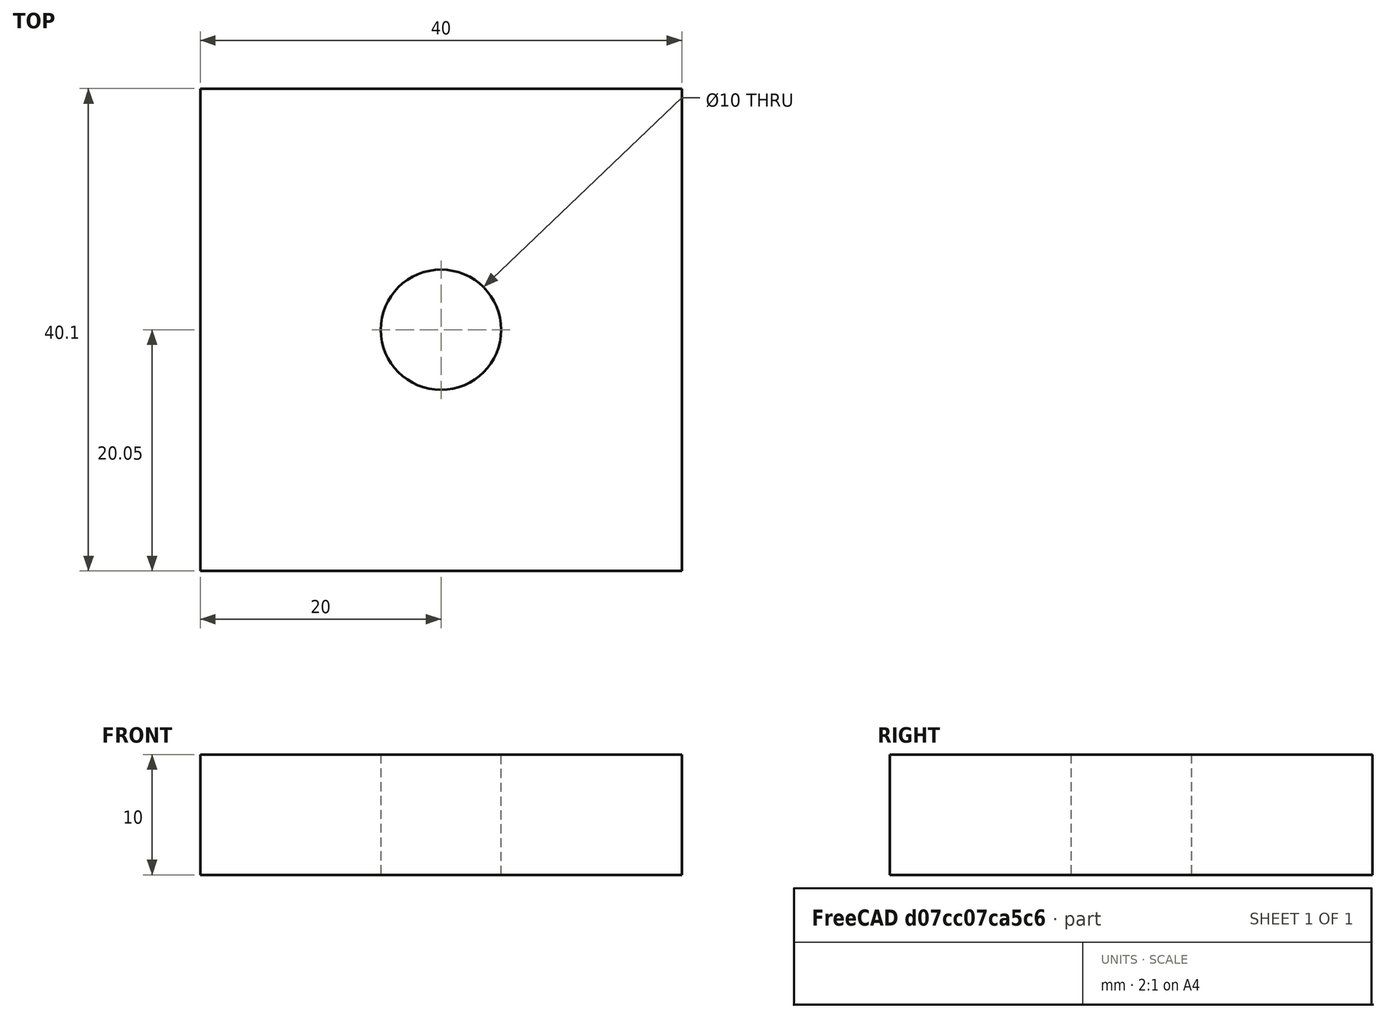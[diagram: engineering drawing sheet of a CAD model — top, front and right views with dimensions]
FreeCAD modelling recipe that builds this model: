
FCSTD DOCUMENT  (FreeCAD 0.20R29410 (Git))
Label: mola
License: All rights reserved
LicenseURL: http://en.wikipedia.org/wiki/All_rights_reserved
objects: Sketcher::SketchObject×1, Part::Extrusion×1
note: 2 computed .brp shape members not serialized (recipe doc carries the construction recipe); baked Part::Feature solids carry a one-line shape summary decoded from their .brp

FEATURE [Sketcher::SketchObject] Sketch
  FullyConstrained = true
  sketch-geometry (5):
    g0: LineSegment StartX=-20 StartY=20.045 StartZ=0 EndX=20 EndY=20.045 EndZ=0
    g1: LineSegment StartX=20 StartY=20.045 StartZ=0 EndX=20 EndY=-20.045 EndZ=0
    g2: LineSegment StartX=20 StartY=-20.045 StartZ=0 EndX=-20 EndY=-20.045 EndZ=0
    g3: LineSegment StartX=-20 StartY=-20.045 StartZ=0 EndX=-20 EndY=20.045 EndZ=0
    g4: Circle CenterX=0 CenterY=0 CenterZ=0 NormalX=0 NormalY=0 NormalZ=1 AngleXU=0 Radius=5
  constraints (13):
    c: Coincident(g0,g1)
    c: Coincident(g1,g2)
    c: Coincident(g2,g3)
    c: Coincident(g3,g0)
    c: Horizontal(g0)
    c: Horizontal(g2)
    c: Vertical(g1)
    c: Vertical(g3)
    c: Symmetric(g1,g0,g-1)
    c: DistanceX(g0,g0) = 40  'a'
    c: DistanceY(g1,g1) = 40.09  'b'
    c: Diameter(g4) = 10  'd'
    c: Coincident(g4,g-1)
FEATURE [Part::Extrusion] Extrude
  Base = -> Sketch
  Dir = (0,0,1)
  DirMode = 2
  FaceMakerClass = Part::FaceMakerBullseye
  LengthFwd = 10
  LengthRev = 0
  Solid = true
  Symmetric = false
